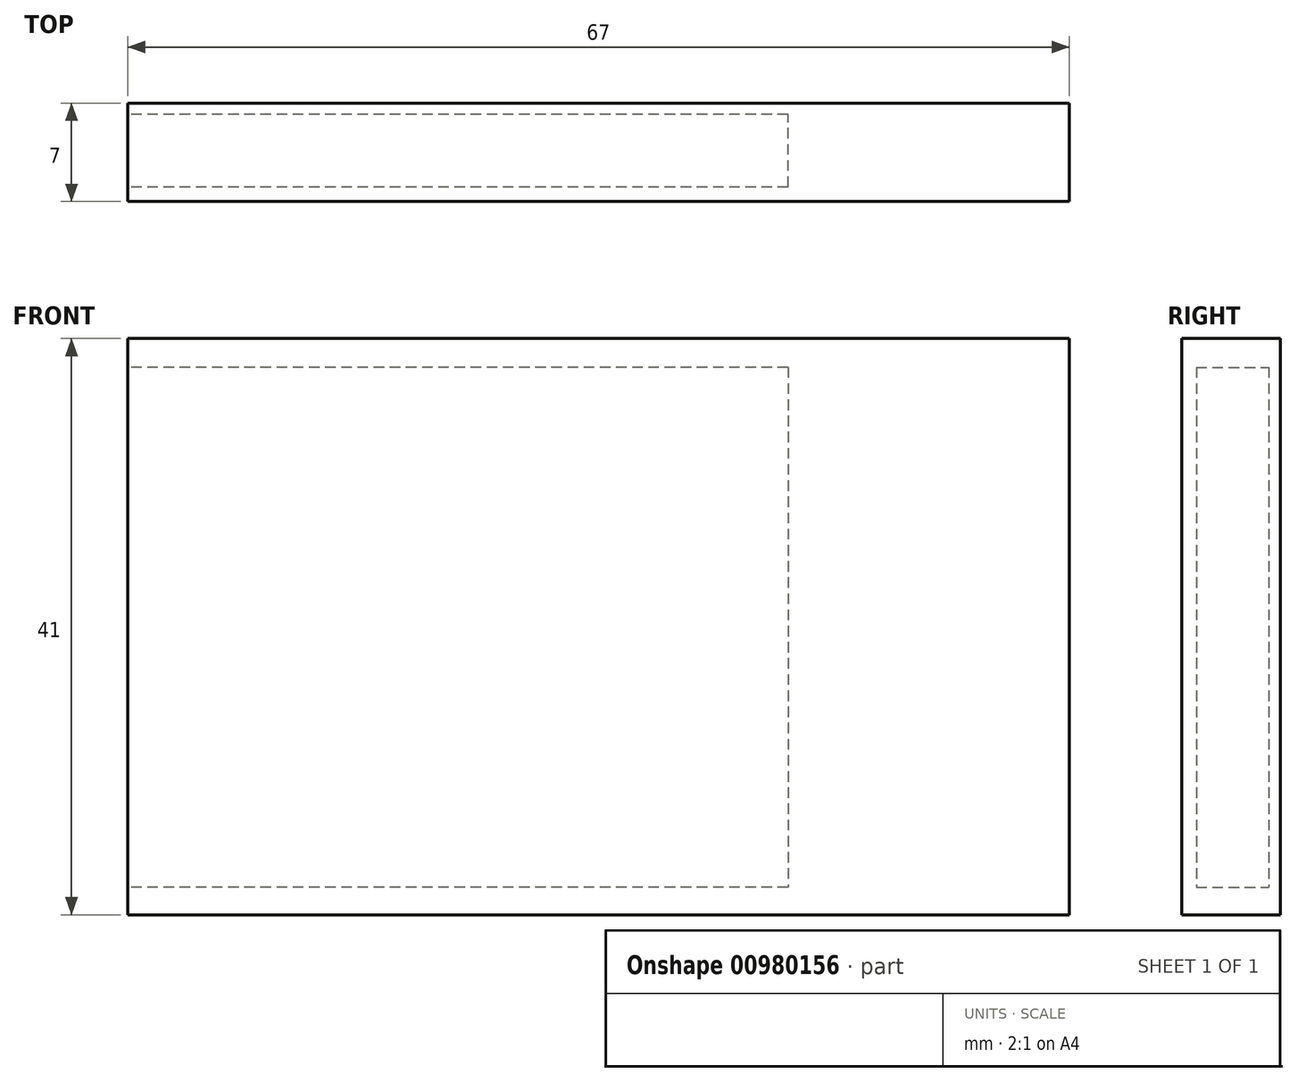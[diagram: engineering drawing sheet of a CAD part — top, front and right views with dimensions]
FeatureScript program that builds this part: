
annotation { "Feature Type Name" : "Feature", "Feature Type Description" : "" }
export const myFeature = defineFeature(function(context is Context, id is Id, definition is map)
    precondition{}
    {
        {
            var Q0;
            Q0=qCreatedBy(makeId("Front.planeOp"),FACE);
            var sketch = newSketch(context, id + "F0", { "sketchPlane" : qUnion([Q0])});
            skLineSegment(sketch, "E0.bottom", {"start": v(46.7, 85.72) * mm, "end": v(-20.3, 85.72) * mm});
            skLineSegment(sketch, "E0.top", {"start": v(46.7, 44.72) * mm, "end": v(-20.3, 44.72) * mm});
            skLineSegment(sketch, "E0.left", {"start": v(46.7, 85.72) * mm, "end": v(46.7, 44.72) * mm});
            skLineSegment(sketch, "E0.right", {"start": v(-20.3, 85.72) * mm, "end": v(-20.3, 44.72) * mm});
            skSolve(sketch);
        }
        {
            var Q0;
            Q0=makeQuery(id+"F0.imprint","IMPRINT",FACE,{"disambiguationData":[TD([[makeQuery(id+"F0.imprint","IMPRINT",EDGE,{"derivedFrom":sQuery(id+"F0.wireOp",EDGE,"E0.bottom")}),1.0]])]});
            extrude(context, id + "F1", {"entities" : qUnion([Q0]), "depth" : 7 * mm, "offsetDistance" : 25 * mm});
        }
        {
            var Q0;
            Q0=makeQuery(id+"F1.opExtrude","SWEPT_FACE",FACE,{"disambiguationData":[OSD([sQuery(id+"F0.wireOp",EDGE,"E0.right")])]});
            var sketch = newSketch(context, id + "F2", { "sketchPlane" : qUnion([Q0])});
            skLineSegment(sketch, "E1", {"start": v(3.5, 85.72) * mm, "end": v(3.5, 44.72) * mm, "construction": true});
            skLineSegment(sketch, "E2", {"start": v(7, 65.22) * mm, "end": v(0, 65.22) * mm, "construction": true});
            skSolve(sketch);
        }
        {
            var Q0;
            {var subQ0=sQuery(id+"F0.wireOp",EDGE,"E0.right");Q0=makeQuery(id+"F2.imprint","IMPRINT",FACE,{"disambiguationData":[TD([[makeQuery(id+"F2.imprint","IMPRINT",EDGE,{"derivedFrom":makeQuery(id+"F1.opExtrude","CAP_EDGE",EDGE,{"disambiguationData":[OSD([subQ0])],"isStart":true})}),1.0]])]});}
            var sketch = newSketch(context, id + "F3", { "sketchPlane" : qUnion([Q0])});
            skLineSegment(sketch, "E3.bottom", {"start": v(5.97, 83.68) * mm, "end": v(0.8, 83.68) * mm});
            skLineSegment(sketch, "E3.top", {"start": v(5.97, 46.68) * mm, "end": v(0.8, 46.68) * mm});
            skLineSegment(sketch, "E3.left", {"start": v(5.97, 83.68) * mm, "end": v(5.97, 46.68) * mm});
            skLineSegment(sketch, "E3.right", {"start": v(0.8, 83.68) * mm, "end": v(0.8, 46.68) * mm});
            skLineSegment(sketch, "E4", {"start": v(5.97, 65.18) * mm, "end": v(0.8, 65.18) * mm, "construction": true});
            skLineSegment(sketch, "E5", {"start": v(3.38, 83.68) * mm, "end": v(3.38, 46.68) * mm, "construction": true});
            skSolve(sketch);
        }
        {
            var Q0;
            Q0=makeQuery(id+"F3.imprint","IMPRINT",FACE,{"disambiguationData":[TD([[makeQuery(id+"F3.imprint","IMPRINT",EDGE,{"derivedFrom":sQuery(id+"F3.wireOp",EDGE,"E3.bottom")}),1.0]])]});
            extrude(context, id + "F4", {"entities" : qUnion([Q0]), "operationType" : NewBodyOperationType.REMOVE, "oppositeDirection" : true, "depth" : 47 * mm, "offsetDistance" : 25 * mm});
        }
    });
